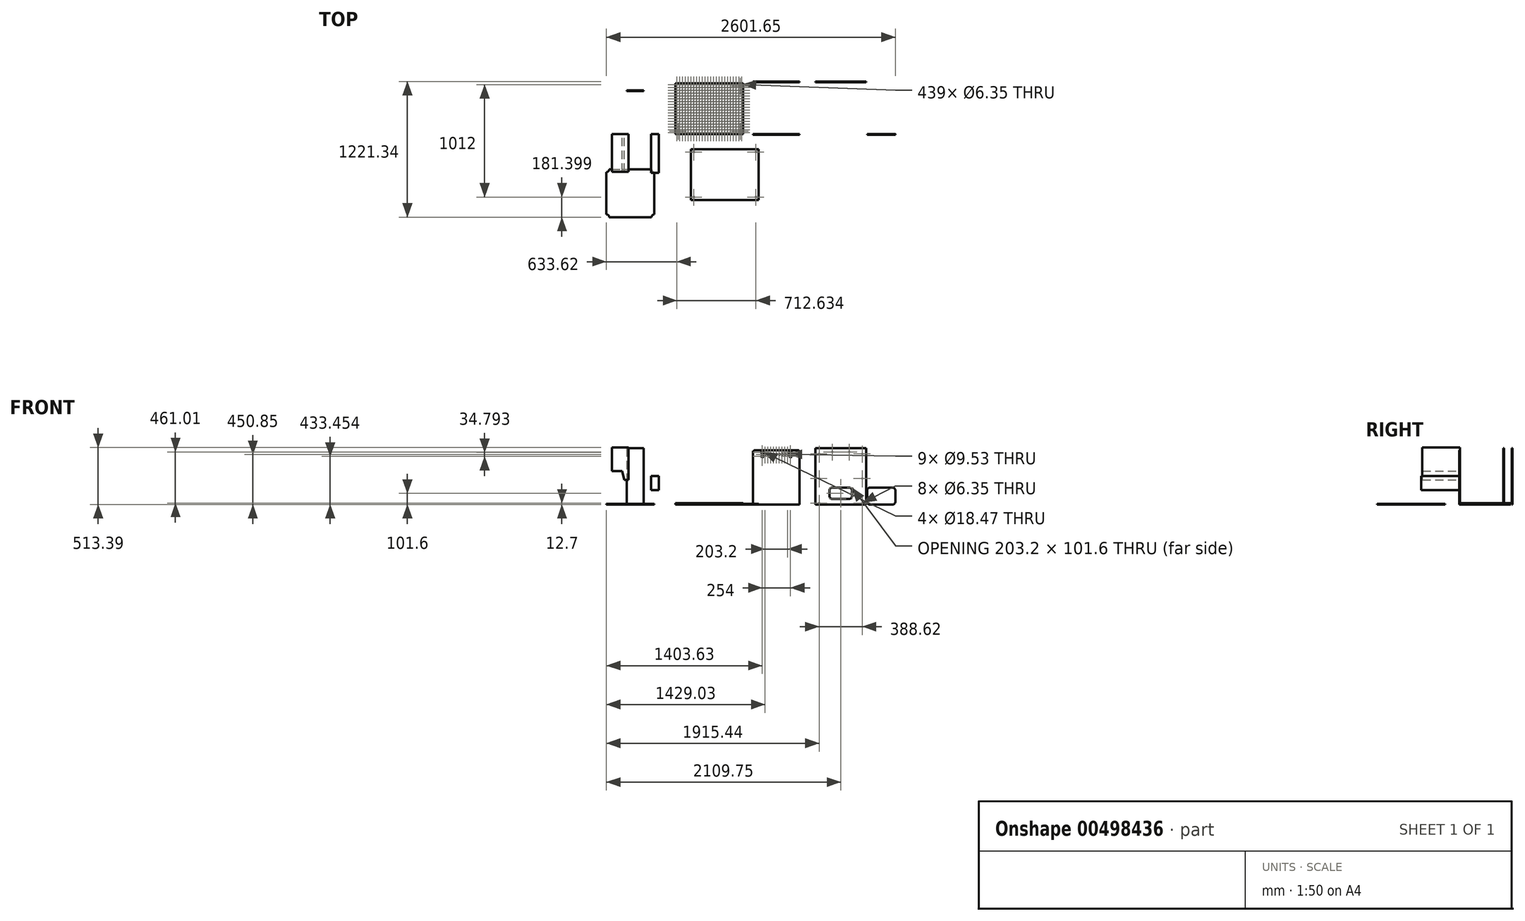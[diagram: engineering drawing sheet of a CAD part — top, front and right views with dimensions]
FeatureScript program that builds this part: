
annotation { "Feature Type Name" : "Feature", "Feature Type Description" : "" }
export const myFeature = defineFeature(function(context is Context, id is Id, definition is map)
    precondition{}
    {
        {
            var Q0;
            Q0=qCreatedBy(makeId("Top.planeOp"),FACE);
            var sketch = newSketch(context, id + "F0", { "sketchPlane" : qUnion([Q0])});
            skLineSegment(sketch, "E0.bottom", {"start": v(0, 0) * mm, "end": v(609.6, 0) * mm});
            skLineSegment(sketch, "E0.top", {"start": v(0, 457.2) * mm, "end": v(609.6, 457.2) * mm});
            skLineSegment(sketch, "E0.left", {"start": v(0, 0) * mm, "end": v(0, 457.2) * mm});
            skLineSegment(sketch, "E0.right", {"start": v(609.6, 0) * mm, "end": v(609.6, 457.2) * mm});
            skCircle(sketch, "E1", {"center": v(12.7, 444.5) * mm, "radius": 3.17 * mm});
            skCircle(sketch, "E2.0.1.0", {"center": v(12.7, 419.1) * mm, "radius": 3.17 * mm});
            skCircle(sketch, "E2.0.2.0", {"center": v(12.7, 393.7) * mm, "radius": 3.17 * mm});
            skCircle(sketch, "E2.0.3.0", {"center": v(12.7, 368.3) * mm, "radius": 3.17 * mm});
            skCircle(sketch, "E2.0.4.0", {"center": v(12.7, 342.9) * mm, "radius": 3.17 * mm});
            skCircle(sketch, "E2.0.5.0", {"center": v(12.7, 317.5) * mm, "radius": 3.17 * mm});
            skCircle(sketch, "E2.0.6.0", {"center": v(12.7, 292.1) * mm, "radius": 3.17 * mm});
            skCircle(sketch, "E2.0.7.0", {"center": v(12.7, 266.7) * mm, "radius": 3.17 * mm});
            skCircle(sketch, "E2.1.0.0", {"center": v(38.1, 444.5) * mm, "radius": 3.17 * mm});
            skCircle(sketch, "E2.1.1.0", {"center": v(38.1, 419.1) * mm, "radius": 3.17 * mm});
            skCircle(sketch, "E2.1.2.0", {"center": v(38.1, 393.7) * mm, "radius": 3.17 * mm});
            skCircle(sketch, "E2.1.3.0", {"center": v(38.1, 368.3) * mm, "radius": 3.17 * mm});
            skCircle(sketch, "E2.1.4.0", {"center": v(38.1, 342.9) * mm, "radius": 3.17 * mm});
            skCircle(sketch, "E2.1.5.0", {"center": v(38.1, 317.5) * mm, "radius": 3.17 * mm});
            skCircle(sketch, "E2.1.6.0", {"center": v(38.1, 292.1) * mm, "radius": 3.17 * mm});
            skCircle(sketch, "E2.1.7.0", {"center": v(38.1, 266.7) * mm, "radius": 3.17 * mm});
            skCircle(sketch, "E2.2.0.0", {"center": v(63.5, 444.5) * mm, "radius": 3.17 * mm});
            skCircle(sketch, "E2.2.1.0", {"center": v(63.5, 419.1) * mm, "radius": 3.17 * mm});
            skCircle(sketch, "E2.2.2.0", {"center": v(63.5, 393.7) * mm, "radius": 3.17 * mm});
            skCircle(sketch, "E2.2.3.0", {"center": v(63.5, 368.3) * mm, "radius": 3.17 * mm});
            skCircle(sketch, "E2.2.4.0", {"center": v(63.5, 342.9) * mm, "radius": 3.17 * mm});
            skCircle(sketch, "E2.2.5.0", {"center": v(63.5, 317.5) * mm, "radius": 3.17 * mm});
            skCircle(sketch, "E2.2.6.0", {"center": v(63.5, 292.1) * mm, "radius": 3.17 * mm});
            skCircle(sketch, "E2.2.7.0", {"center": v(63.5, 266.7) * mm, "radius": 3.17 * mm});
            skCircle(sketch, "E2.3.0.0", {"center": v(88.9, 444.5) * mm, "radius": 3.17 * mm});
            skCircle(sketch, "E2.3.1.0", {"center": v(88.9, 419.1) * mm, "radius": 3.17 * mm});
            skCircle(sketch, "E2.3.2.0", {"center": v(88.9, 393.7) * mm, "radius": 3.17 * mm});
            skCircle(sketch, "E2.3.3.0", {"center": v(88.9, 368.3) * mm, "radius": 3.17 * mm});
            skCircle(sketch, "E2.3.4.0", {"center": v(88.9, 342.9) * mm, "radius": 3.17 * mm});
            skCircle(sketch, "E2.3.5.0", {"center": v(88.9, 317.5) * mm, "radius": 3.17 * mm});
            skCircle(sketch, "E2.3.6.0", {"center": v(88.9, 292.1) * mm, "radius": 3.17 * mm});
            skCircle(sketch, "E2.3.7.0", {"center": v(88.9, 266.7) * mm, "radius": 3.17 * mm});
            skCircle(sketch, "E2.4.0.0", {"center": v(114.3, 444.5) * mm, "radius": 3.17 * mm});
            skCircle(sketch, "E2.4.1.0", {"center": v(114.3, 419.1) * mm, "radius": 3.17 * mm});
            skCircle(sketch, "E2.4.2.0", {"center": v(114.3, 393.7) * mm, "radius": 3.17 * mm});
            skCircle(sketch, "E2.4.3.0", {"center": v(114.3, 368.3) * mm, "radius": 3.17 * mm});
            skCircle(sketch, "E2.4.4.0", {"center": v(114.3, 342.9) * mm, "radius": 3.17 * mm});
            skCircle(sketch, "E2.4.5.0", {"center": v(114.3, 317.5) * mm, "radius": 3.17 * mm});
            skCircle(sketch, "E2.4.6.0", {"center": v(114.3, 292.1) * mm, "radius": 3.17 * mm});
            skCircle(sketch, "E2.4.7.0", {"center": v(114.3, 266.7) * mm, "radius": 3.17 * mm});
            skCircle(sketch, "E2.5.0.0", {"center": v(139.7, 444.5) * mm, "radius": 3.17 * mm});
            skCircle(sketch, "E2.5.1.0", {"center": v(139.7, 419.1) * mm, "radius": 3.17 * mm});
            skCircle(sketch, "E2.5.2.0", {"center": v(139.7, 393.7) * mm, "radius": 3.17 * mm});
            skCircle(sketch, "E2.5.3.0", {"center": v(139.7, 368.3) * mm, "radius": 3.17 * mm});
            skCircle(sketch, "E2.5.4.0", {"center": v(139.7, 342.9) * mm, "radius": 3.17 * mm});
            skCircle(sketch, "E2.5.5.0", {"center": v(139.7, 317.5) * mm, "radius": 3.17 * mm});
            skCircle(sketch, "E2.5.6.0", {"center": v(139.7, 292.1) * mm, "radius": 3.17 * mm});
            skCircle(sketch, "E2.5.7.0", {"center": v(139.7, 266.7) * mm, "radius": 3.17 * mm});
            skCircle(sketch, "E2.6.0.0", {"center": v(165.1, 444.5) * mm, "radius": 3.17 * mm});
            skCircle(sketch, "E2.6.1.0", {"center": v(165.1, 419.1) * mm, "radius": 3.17 * mm});
            skCircle(sketch, "E2.6.2.0", {"center": v(165.1, 393.7) * mm, "radius": 3.17 * mm});
            skCircle(sketch, "E2.6.3.0", {"center": v(165.1, 368.3) * mm, "radius": 3.17 * mm});
            skCircle(sketch, "E2.6.4.0", {"center": v(165.1, 342.9) * mm, "radius": 3.17 * mm});
            skCircle(sketch, "E2.6.5.0", {"center": v(165.1, 317.5) * mm, "radius": 3.17 * mm});
            skCircle(sketch, "E2.6.6.0", {"center": v(165.1, 292.1) * mm, "radius": 3.17 * mm});
            skCircle(sketch, "E2.6.7.0", {"center": v(165.1, 266.7) * mm, "radius": 3.17 * mm});
            skCircle(sketch, "E2.7.0.0", {"center": v(190.5, 444.5) * mm, "radius": 3.17 * mm});
            skCircle(sketch, "E2.7.1.0", {"center": v(190.5, 419.1) * mm, "radius": 3.17 * mm});
            skCircle(sketch, "E2.7.2.0", {"center": v(190.5, 393.7) * mm, "radius": 3.17 * mm});
            skCircle(sketch, "E2.7.3.0", {"center": v(190.5, 368.3) * mm, "radius": 3.17 * mm});
            skCircle(sketch, "E2.7.4.0", {"center": v(190.5, 342.9) * mm, "radius": 3.17 * mm});
            skCircle(sketch, "E2.7.5.0", {"center": v(190.5, 317.5) * mm, "radius": 3.17 * mm});
            skCircle(sketch, "E2.7.6.0", {"center": v(190.5, 292.1) * mm, "radius": 3.17 * mm});
            skCircle(sketch, "E2.7.7.0", {"center": v(190.5, 266.7) * mm, "radius": 3.17 * mm});
            skCircle(sketch, "E2.8.0.0", {"center": v(215.9, 444.5) * mm, "radius": 3.17 * mm});
            skCircle(sketch, "E2.8.1.0", {"center": v(215.9, 419.1) * mm, "radius": 3.17 * mm});
            skCircle(sketch, "E2.8.2.0", {"center": v(215.9, 393.7) * mm, "radius": 3.17 * mm});
            skCircle(sketch, "E2.8.3.0", {"center": v(215.9, 368.3) * mm, "radius": 3.17 * mm});
            skCircle(sketch, "E2.8.4.0", {"center": v(215.9, 342.9) * mm, "radius": 3.17 * mm});
            skCircle(sketch, "E2.8.5.0", {"center": v(215.9, 317.5) * mm, "radius": 3.17 * mm});
            skCircle(sketch, "E2.8.6.0", {"center": v(215.9, 292.1) * mm, "radius": 3.17 * mm});
            skCircle(sketch, "E2.8.7.0", {"center": v(215.9, 266.7) * mm, "radius": 3.17 * mm});
            skCircle(sketch, "E2.9.0.0", {"center": v(241.3, 444.5) * mm, "radius": 3.17 * mm});
            skCircle(sketch, "E2.9.1.0", {"center": v(241.3, 419.1) * mm, "radius": 3.17 * mm});
            skCircle(sketch, "E2.9.2.0", {"center": v(241.3, 393.7) * mm, "radius": 3.17 * mm});
            skCircle(sketch, "E2.9.3.0", {"center": v(241.3, 368.3) * mm, "radius": 3.17 * mm});
            skCircle(sketch, "E2.9.4.0", {"center": v(241.3, 342.9) * mm, "radius": 3.17 * mm});
            skCircle(sketch, "E2.9.5.0", {"center": v(241.3, 317.5) * mm, "radius": 3.17 * mm});
            skCircle(sketch, "E2.9.6.0", {"center": v(241.3, 292.1) * mm, "radius": 3.17 * mm});
            skCircle(sketch, "E2.9.7.0", {"center": v(241.3, 266.7) * mm, "radius": 3.17 * mm});
            skCircle(sketch, "E2.10.0.0", {"center": v(266.7, 444.5) * mm, "radius": 3.17 * mm});
            skCircle(sketch, "E2.10.1.0", {"center": v(266.7, 419.1) * mm, "radius": 3.17 * mm});
            skCircle(sketch, "E2.10.2.0", {"center": v(266.7, 393.7) * mm, "radius": 3.17 * mm});
            skCircle(sketch, "E2.10.3.0", {"center": v(266.7, 368.3) * mm, "radius": 3.17 * mm});
            skCircle(sketch, "E2.10.4.0", {"center": v(266.7, 342.9) * mm, "radius": 3.17 * mm});
            skCircle(sketch, "E2.10.5.0", {"center": v(266.7, 317.5) * mm, "radius": 3.17 * mm});
            skCircle(sketch, "E2.10.6.0", {"center": v(266.7, 292.1) * mm, "radius": 3.17 * mm});
            skCircle(sketch, "E2.10.7.0", {"center": v(266.7, 266.7) * mm, "radius": 3.17 * mm});
            skCircle(sketch, "E2.11.0.0", {"center": v(292.1, 444.5) * mm, "radius": 3.17 * mm});
            skCircle(sketch, "E2.11.1.0", {"center": v(292.1, 419.1) * mm, "radius": 3.17 * mm});
            skCircle(sketch, "E2.11.2.0", {"center": v(292.1, 393.7) * mm, "radius": 3.17 * mm});
            skCircle(sketch, "E2.11.3.0", {"center": v(292.1, 368.3) * mm, "radius": 3.17 * mm});
            skCircle(sketch, "E2.11.4.0", {"center": v(292.1, 342.9) * mm, "radius": 3.17 * mm});
            skCircle(sketch, "E2.11.5.0", {"center": v(292.1, 317.5) * mm, "radius": 3.17 * mm});
            skCircle(sketch, "E2.11.6.0", {"center": v(292.1, 292.1) * mm, "radius": 3.17 * mm});
            skCircle(sketch, "E2.11.7.0", {"center": v(292.1, 266.7) * mm, "radius": 3.17 * mm});
            skCircle(sketch, "E2.12.0.0", {"center": v(317.5, 444.5) * mm, "radius": 3.17 * mm});
            skCircle(sketch, "E2.12.1.0", {"center": v(317.5, 419.1) * mm, "radius": 3.17 * mm});
            skCircle(sketch, "E2.12.2.0", {"center": v(317.5, 393.7) * mm, "radius": 3.17 * mm});
            skCircle(sketch, "E2.12.3.0", {"center": v(317.5, 368.3) * mm, "radius": 3.17 * mm});
            skCircle(sketch, "E2.12.4.0", {"center": v(317.5, 342.9) * mm, "radius": 3.17 * mm});
            skCircle(sketch, "E2.12.5.0", {"center": v(317.5, 317.5) * mm, "radius": 3.17 * mm});
            skCircle(sketch, "E2.12.6.0", {"center": v(317.5, 292.1) * mm, "radius": 3.17 * mm});
            skCircle(sketch, "E2.12.7.0", {"center": v(317.5, 266.7) * mm, "radius": 3.17 * mm});
            skCircle(sketch, "E2.13.0.0", {"center": v(342.9, 444.5) * mm, "radius": 3.17 * mm});
            skCircle(sketch, "E2.13.1.0", {"center": v(342.9, 419.1) * mm, "radius": 3.17 * mm});
            skCircle(sketch, "E2.13.2.0", {"center": v(342.9, 393.7) * mm, "radius": 3.17 * mm});
            skCircle(sketch, "E2.13.3.0", {"center": v(342.9, 368.3) * mm, "radius": 3.17 * mm});
            skCircle(sketch, "E2.13.4.0", {"center": v(342.9, 342.9) * mm, "radius": 3.17 * mm});
            skCircle(sketch, "E2.13.5.0", {"center": v(342.9, 317.5) * mm, "radius": 3.17 * mm});
            skCircle(sketch, "E2.13.6.0", {"center": v(342.9, 292.1) * mm, "radius": 3.17 * mm});
            skCircle(sketch, "E2.13.7.0", {"center": v(342.9, 266.7) * mm, "radius": 3.17 * mm});
            skCircle(sketch, "E2.14.0.0", {"center": v(368.3, 444.5) * mm, "radius": 3.17 * mm});
            skCircle(sketch, "E2.14.1.0", {"center": v(368.3, 419.1) * mm, "radius": 3.17 * mm});
            skCircle(sketch, "E2.14.2.0", {"center": v(368.3, 393.7) * mm, "radius": 3.17 * mm});
            skCircle(sketch, "E2.14.3.0", {"center": v(368.3, 368.3) * mm, "radius": 3.17 * mm});
            skCircle(sketch, "E2.14.4.0", {"center": v(368.3, 342.9) * mm, "radius": 3.17 * mm});
            skCircle(sketch, "E2.14.5.0", {"center": v(368.3, 317.5) * mm, "radius": 3.17 * mm});
            skCircle(sketch, "E2.14.6.0", {"center": v(368.3, 292.1) * mm, "radius": 3.17 * mm});
            skCircle(sketch, "E2.14.7.0", {"center": v(368.3, 266.7) * mm, "radius": 3.17 * mm});
            skCircle(sketch, "E2.15.0.0", {"center": v(393.7, 444.5) * mm, "radius": 3.17 * mm});
            skCircle(sketch, "E2.15.1.0", {"center": v(393.7, 419.1) * mm, "radius": 3.17 * mm});
            skCircle(sketch, "E2.15.2.0", {"center": v(393.7, 393.7) * mm, "radius": 3.17 * mm});
            skCircle(sketch, "E2.15.3.0", {"center": v(393.7, 368.3) * mm, "radius": 3.17 * mm});
            skCircle(sketch, "E2.15.4.0", {"center": v(393.7, 342.9) * mm, "radius": 3.17 * mm});
            skCircle(sketch, "E2.15.5.0", {"center": v(393.7, 317.5) * mm, "radius": 3.17 * mm});
            skCircle(sketch, "E2.15.6.0", {"center": v(393.7, 292.1) * mm, "radius": 3.17 * mm});
            skCircle(sketch, "E2.15.7.0", {"center": v(393.7, 266.7) * mm, "radius": 3.17 * mm});
            skCircle(sketch, "E2.16.0.0", {"center": v(419.1, 444.5) * mm, "radius": 3.17 * mm});
            skCircle(sketch, "E2.16.1.0", {"center": v(419.1, 419.1) * mm, "radius": 3.17 * mm});
            skCircle(sketch, "E2.16.2.0", {"center": v(419.1, 393.7) * mm, "radius": 3.17 * mm});
            skCircle(sketch, "E2.16.3.0", {"center": v(419.1, 368.3) * mm, "radius": 3.17 * mm});
            skCircle(sketch, "E2.16.4.0", {"center": v(419.1, 342.9) * mm, "radius": 3.17 * mm});
            skCircle(sketch, "E2.16.5.0", {"center": v(419.1, 317.5) * mm, "radius": 3.17 * mm});
            skCircle(sketch, "E2.16.6.0", {"center": v(419.1, 292.1) * mm, "radius": 3.17 * mm});
            skCircle(sketch, "E2.16.7.0", {"center": v(419.1, 266.7) * mm, "radius": 3.17 * mm});
            skCircle(sketch, "E2.17.0.0", {"center": v(444.5, 444.5) * mm, "radius": 3.17 * mm});
            skCircle(sketch, "E2.17.1.0", {"center": v(444.5, 419.1) * mm, "radius": 3.17 * mm});
            skCircle(sketch, "E2.17.2.0", {"center": v(444.5, 393.7) * mm, "radius": 3.17 * mm});
            skCircle(sketch, "E2.17.3.0", {"center": v(444.5, 368.3) * mm, "radius": 3.17 * mm});
            skCircle(sketch, "E2.17.4.0", {"center": v(444.5, 342.9) * mm, "radius": 3.17 * mm});
            skCircle(sketch, "E2.17.5.0", {"center": v(444.5, 317.5) * mm, "radius": 3.17 * mm});
            skCircle(sketch, "E2.17.6.0", {"center": v(444.5, 292.1) * mm, "radius": 3.17 * mm});
            skCircle(sketch, "E2.17.7.0", {"center": v(444.5, 266.7) * mm, "radius": 3.17 * mm});
            skCircle(sketch, "E2.18.0.0", {"center": v(469.9, 444.5) * mm, "radius": 3.17 * mm});
            skCircle(sketch, "E2.18.1.0", {"center": v(469.9, 419.1) * mm, "radius": 3.17 * mm});
            skCircle(sketch, "E2.18.2.0", {"center": v(469.9, 393.7) * mm, "radius": 3.17 * mm});
            skCircle(sketch, "E2.18.3.0", {"center": v(469.9, 368.3) * mm, "radius": 3.17 * mm});
            skCircle(sketch, "E2.18.4.0", {"center": v(469.9, 342.9) * mm, "radius": 3.17 * mm});
            skCircle(sketch, "E2.18.5.0", {"center": v(469.9, 317.5) * mm, "radius": 3.17 * mm});
            skCircle(sketch, "E2.18.6.0", {"center": v(469.9, 292.1) * mm, "radius": 3.17 * mm});
            skCircle(sketch, "E2.18.7.0", {"center": v(469.9, 266.7) * mm, "radius": 3.17 * mm});
            skCircle(sketch, "E2.19.0.0", {"center": v(495.3, 444.5) * mm, "radius": 3.17 * mm});
            skCircle(sketch, "E2.19.1.0", {"center": v(495.3, 419.1) * mm, "radius": 3.17 * mm});
            skCircle(sketch, "E2.19.2.0", {"center": v(495.3, 393.7) * mm, "radius": 3.17 * mm});
            skCircle(sketch, "E2.19.3.0", {"center": v(495.3, 368.3) * mm, "radius": 3.17 * mm});
            skCircle(sketch, "E2.19.4.0", {"center": v(495.3, 342.9) * mm, "radius": 3.17 * mm});
            skCircle(sketch, "E2.19.5.0", {"center": v(495.3, 317.5) * mm, "radius": 3.17 * mm});
            skCircle(sketch, "E2.19.6.0", {"center": v(495.3, 292.1) * mm, "radius": 3.17 * mm});
            skCircle(sketch, "E2.19.7.0", {"center": v(495.3, 266.7) * mm, "radius": 3.17 * mm});
            skCircle(sketch, "E2.20.0.0", {"center": v(520.7, 444.5) * mm, "radius": 3.17 * mm});
            skCircle(sketch, "E2.20.1.0", {"center": v(520.7, 419.1) * mm, "radius": 3.17 * mm});
            skCircle(sketch, "E2.20.2.0", {"center": v(520.7, 393.7) * mm, "radius": 3.17 * mm});
            skCircle(sketch, "E2.20.3.0", {"center": v(520.7, 368.3) * mm, "radius": 3.17 * mm});
            skCircle(sketch, "E2.20.4.0", {"center": v(520.7, 342.9) * mm, "radius": 3.17 * mm});
            skCircle(sketch, "E2.20.5.0", {"center": v(520.7, 317.5) * mm, "radius": 3.17 * mm});
            skCircle(sketch, "E2.20.6.0", {"center": v(520.7, 292.1) * mm, "radius": 3.17 * mm});
            skCircle(sketch, "E2.20.7.0", {"center": v(520.7, 266.7) * mm, "radius": 3.17 * mm});
            skCircle(sketch, "E2.21.0.0", {"center": v(546.1, 444.5) * mm, "radius": 3.17 * mm});
            skCircle(sketch, "E2.21.1.0", {"center": v(546.1, 419.1) * mm, "radius": 3.17 * mm});
            skCircle(sketch, "E2.21.2.0", {"center": v(546.1, 393.7) * mm, "radius": 3.17 * mm});
            skCircle(sketch, "E2.21.3.0", {"center": v(546.1, 368.3) * mm, "radius": 3.17 * mm});
            skCircle(sketch, "E2.21.4.0", {"center": v(546.1, 342.9) * mm, "radius": 3.17 * mm});
            skCircle(sketch, "E2.21.5.0", {"center": v(546.1, 317.5) * mm, "radius": 3.17 * mm});
            skCircle(sketch, "E2.21.6.0", {"center": v(546.1, 292.1) * mm, "radius": 3.17 * mm});
            skCircle(sketch, "E2.21.7.0", {"center": v(546.1, 266.7) * mm, "radius": 3.17 * mm});
            skCircle(sketch, "E2.22.0.0", {"center": v(571.5, 444.5) * mm, "radius": 3.17 * mm});
            skCircle(sketch, "E2.22.1.0", {"center": v(571.5, 419.1) * mm, "radius": 3.17 * mm});
            skCircle(sketch, "E2.22.2.0", {"center": v(571.5, 393.7) * mm, "radius": 3.17 * mm});
            skCircle(sketch, "E2.22.3.0", {"center": v(571.5, 368.3) * mm, "radius": 3.17 * mm});
            skCircle(sketch, "E2.22.4.0", {"center": v(571.5, 342.9) * mm, "radius": 3.17 * mm});
            skCircle(sketch, "E2.22.5.0", {"center": v(571.5, 317.5) * mm, "radius": 3.17 * mm});
            skCircle(sketch, "E2.22.6.0", {"center": v(571.5, 292.1) * mm, "radius": 3.17 * mm});
            skCircle(sketch, "E2.22.7.0", {"center": v(571.5, 266.7) * mm, "radius": 3.17 * mm});
            skLineSegment(sketch, "E2.direction1", {"start": v(12.7, 444.5) * mm, "end": v(38.1, 444.5) * mm, "construction": true});
            skLineSegment(sketch, "E2.direction2", {"start": v(12.7, 444.5) * mm, "end": v(12.7, 419.1) * mm, "construction": true});
            skCircle(sketch, "E3.0.23.0", {"center": v(596.9, 444.5) * mm, "radius": 3.17 * mm});
            skCircle(sketch, "E3.0.23.1", {"center": v(596.9, 419.1) * mm, "radius": 3.17 * mm});
            skCircle(sketch, "E3.0.23.2", {"center": v(596.9, 393.7) * mm, "radius": 3.17 * mm});
            skCircle(sketch, "E3.0.23.3", {"center": v(596.9, 368.3) * mm, "radius": 3.17 * mm});
            skCircle(sketch, "E3.0.23.4", {"center": v(596.9, 342.9) * mm, "radius": 3.17 * mm});
            skCircle(sketch, "E3.0.23.5", {"center": v(596.9, 317.5) * mm, "radius": 3.17 * mm});
            skCircle(sketch, "E3.0.23.6", {"center": v(596.9, 292.1) * mm, "radius": 3.17 * mm});
            skCircle(sketch, "E3.0.23.7", {"center": v(596.9, 266.7) * mm, "radius": 3.17 * mm});
            skCircle(sketch, "E4.0.0.8", {"center": v(12.7, 241.3) * mm, "radius": 3.17 * mm});
            skCircle(sketch, "E4.0.0.9", {"center": v(12.7, 215.9) * mm, "radius": 3.17 * mm});
            skCircle(sketch, "E4.0.0.10", {"center": v(12.7, 190.5) * mm, "radius": 3.17 * mm});
            skCircle(sketch, "E4.0.0.11", {"center": v(12.7, 165.1) * mm, "radius": 3.17 * mm});
            skCircle(sketch, "E4.0.0.12", {"center": v(12.7, 139.7) * mm, "radius": 3.17 * mm});
            skCircle(sketch, "E4.0.0.13", {"center": v(12.7, 114.3) * mm, "radius": 3.17 * mm});
            skCircle(sketch, "E4.0.0.14", {"center": v(12.7, 88.9) * mm, "radius": 3.17 * mm});
            skCircle(sketch, "E4.0.0.15", {"center": v(12.7, 63.5) * mm, "radius": 3.17 * mm});
            skCircle(sketch, "E4.0.0.16", {"center": v(12.7, 38.1) * mm, "radius": 3.17 * mm});
            skCircle(sketch, "E4.0.0.17", {"center": v(12.7, 12.7) * mm, "radius": 3.17 * mm});
            skCircle(sketch, "E4.0.1.8", {"center": v(38.1, 241.3) * mm, "radius": 3.17 * mm});
            skCircle(sketch, "E4.0.1.9", {"center": v(38.1, 215.9) * mm, "radius": 3.17 * mm});
            skCircle(sketch, "E4.0.1.10", {"center": v(38.1, 190.5) * mm, "radius": 3.17 * mm});
            skCircle(sketch, "E4.0.1.11", {"center": v(38.1, 165.1) * mm, "radius": 3.17 * mm});
            skCircle(sketch, "E4.0.1.12", {"center": v(38.1, 139.7) * mm, "radius": 3.17 * mm});
            skCircle(sketch, "E4.0.1.13", {"center": v(38.1, 114.3) * mm, "radius": 3.17 * mm});
            skCircle(sketch, "E4.0.1.14", {"center": v(38.1, 88.9) * mm, "radius": 3.17 * mm});
            skCircle(sketch, "E4.0.1.15", {"center": v(38.1, 63.5) * mm, "radius": 3.17 * mm});
            skCircle(sketch, "E4.0.1.16", {"center": v(38.1, 38.1) * mm, "radius": 3.17 * mm});
            skCircle(sketch, "E4.0.1.17", {"center": v(38.1, 12.7) * mm, "radius": 3.17 * mm});
            skCircle(sketch, "E4.0.2.8", {"center": v(63.5, 241.3) * mm, "radius": 3.17 * mm});
            skCircle(sketch, "E4.0.2.9", {"center": v(63.5, 215.9) * mm, "radius": 3.17 * mm});
            skCircle(sketch, "E4.0.2.10", {"center": v(63.5, 190.5) * mm, "radius": 3.17 * mm});
            skCircle(sketch, "E4.0.2.11", {"center": v(63.5, 165.1) * mm, "radius": 3.17 * mm});
            skCircle(sketch, "E4.0.2.12", {"center": v(63.5, 139.7) * mm, "radius": 3.17 * mm});
            skCircle(sketch, "E4.0.2.13", {"center": v(63.5, 114.3) * mm, "radius": 3.17 * mm});
            skCircle(sketch, "E4.0.2.14", {"center": v(63.5, 88.9) * mm, "radius": 3.17 * mm});
            skCircle(sketch, "E4.0.2.15", {"center": v(63.5, 63.5) * mm, "radius": 3.17 * mm});
            skCircle(sketch, "E4.0.2.16", {"center": v(63.5, 38.1) * mm, "radius": 3.17 * mm});
            skCircle(sketch, "E4.0.2.17", {"center": v(63.5, 12.7) * mm, "radius": 3.17 * mm});
            skCircle(sketch, "E4.0.3.8", {"center": v(88.9, 241.3) * mm, "radius": 3.17 * mm});
            skCircle(sketch, "E4.0.3.9", {"center": v(88.9, 215.9) * mm, "radius": 3.17 * mm});
            skCircle(sketch, "E4.0.3.10", {"center": v(88.9, 190.5) * mm, "radius": 3.17 * mm});
            skCircle(sketch, "E4.0.3.11", {"center": v(88.9, 165.1) * mm, "radius": 3.17 * mm});
            skCircle(sketch, "E4.0.3.12", {"center": v(88.9, 139.7) * mm, "radius": 3.17 * mm});
            skCircle(sketch, "E4.0.3.13", {"center": v(88.9, 114.3) * mm, "radius": 3.17 * mm});
            skCircle(sketch, "E4.0.3.14", {"center": v(88.9, 88.9) * mm, "radius": 3.17 * mm});
            skCircle(sketch, "E4.0.3.15", {"center": v(88.9, 63.5) * mm, "radius": 3.17 * mm});
            skCircle(sketch, "E4.0.3.16", {"center": v(88.9, 38.1) * mm, "radius": 3.17 * mm});
            skCircle(sketch, "E4.0.3.17", {"center": v(88.9, 12.7) * mm, "radius": 3.17 * mm});
            skCircle(sketch, "E4.0.4.8", {"center": v(114.3, 241.3) * mm, "radius": 3.17 * mm});
            skCircle(sketch, "E4.0.4.9", {"center": v(114.3, 215.9) * mm, "radius": 3.17 * mm});
            skCircle(sketch, "E4.0.4.10", {"center": v(114.3, 190.5) * mm, "radius": 3.17 * mm});
            skCircle(sketch, "E4.0.4.11", {"center": v(114.3, 165.1) * mm, "radius": 3.17 * mm});
            skCircle(sketch, "E4.0.4.12", {"center": v(114.3, 139.7) * mm, "radius": 3.17 * mm});
            skCircle(sketch, "E4.0.4.13", {"center": v(114.3, 114.3) * mm, "radius": 3.17 * mm});
            skCircle(sketch, "E4.0.4.14", {"center": v(114.3, 88.9) * mm, "radius": 3.17 * mm});
            skCircle(sketch, "E4.0.4.15", {"center": v(114.3, 63.5) * mm, "radius": 3.17 * mm});
            skCircle(sketch, "E4.0.4.16", {"center": v(114.3, 38.1) * mm, "radius": 3.17 * mm});
            skCircle(sketch, "E4.0.4.17", {"center": v(114.3, 12.7) * mm, "radius": 3.17 * mm});
            skCircle(sketch, "E4.0.5.8", {"center": v(139.7, 241.3) * mm, "radius": 3.17 * mm});
            skCircle(sketch, "E4.0.5.9", {"center": v(139.7, 215.9) * mm, "radius": 3.17 * mm});
            skCircle(sketch, "E4.0.5.10", {"center": v(139.7, 190.5) * mm, "radius": 3.17 * mm});
            skCircle(sketch, "E4.0.5.11", {"center": v(139.7, 165.1) * mm, "radius": 3.17 * mm});
            skCircle(sketch, "E4.0.5.12", {"center": v(139.7, 139.7) * mm, "radius": 3.17 * mm});
            skCircle(sketch, "E4.0.5.13", {"center": v(139.7, 114.3) * mm, "radius": 3.17 * mm});
            skCircle(sketch, "E4.0.5.14", {"center": v(139.7, 88.9) * mm, "radius": 3.17 * mm});
            skCircle(sketch, "E4.0.5.15", {"center": v(139.7, 63.5) * mm, "radius": 3.17 * mm});
            skCircle(sketch, "E4.0.5.16", {"center": v(139.7, 38.1) * mm, "radius": 3.17 * mm});
            skCircle(sketch, "E4.0.5.17", {"center": v(139.7, 12.7) * mm, "radius": 3.17 * mm});
            skCircle(sketch, "E4.0.6.8", {"center": v(165.1, 241.3) * mm, "radius": 3.17 * mm});
            skCircle(sketch, "E4.0.6.9", {"center": v(165.1, 215.9) * mm, "radius": 3.17 * mm});
            skCircle(sketch, "E4.0.6.10", {"center": v(165.1, 190.5) * mm, "radius": 3.17 * mm});
            skCircle(sketch, "E4.0.6.11", {"center": v(165.1, 165.1) * mm, "radius": 3.17 * mm});
            skCircle(sketch, "E4.0.6.12", {"center": v(165.1, 139.7) * mm, "radius": 3.17 * mm});
            skCircle(sketch, "E4.0.6.13", {"center": v(165.1, 114.3) * mm, "radius": 3.17 * mm});
            skCircle(sketch, "E4.0.6.14", {"center": v(165.1, 88.9) * mm, "radius": 3.17 * mm});
            skCircle(sketch, "E4.0.6.15", {"center": v(165.1, 63.5) * mm, "radius": 3.17 * mm});
            skCircle(sketch, "E4.0.6.16", {"center": v(165.1, 38.1) * mm, "radius": 3.17 * mm});
            skCircle(sketch, "E4.0.6.17", {"center": v(165.1, 12.7) * mm, "radius": 3.17 * mm});
            skCircle(sketch, "E4.0.7.8", {"center": v(190.5, 241.3) * mm, "radius": 3.17 * mm});
            skCircle(sketch, "E4.0.7.9", {"center": v(190.5, 215.9) * mm, "radius": 3.17 * mm});
            skCircle(sketch, "E4.0.7.10", {"center": v(190.5, 190.5) * mm, "radius": 3.17 * mm});
            skCircle(sketch, "E4.0.7.11", {"center": v(190.5, 165.1) * mm, "radius": 3.17 * mm});
            skCircle(sketch, "E4.0.7.12", {"center": v(190.5, 139.7) * mm, "radius": 3.17 * mm});
            skCircle(sketch, "E4.0.7.13", {"center": v(190.5, 114.3) * mm, "radius": 3.17 * mm});
            skCircle(sketch, "E4.0.7.14", {"center": v(190.5, 88.9) * mm, "radius": 3.17 * mm});
            skCircle(sketch, "E4.0.7.15", {"center": v(190.5, 63.5) * mm, "radius": 3.17 * mm});
            skCircle(sketch, "E4.0.7.16", {"center": v(190.5, 38.1) * mm, "radius": 3.17 * mm});
            skCircle(sketch, "E4.0.7.17", {"center": v(190.5, 12.7) * mm, "radius": 3.17 * mm});
            skCircle(sketch, "E4.0.8.8", {"center": v(215.9, 241.3) * mm, "radius": 3.17 * mm});
            skCircle(sketch, "E4.0.8.9", {"center": v(215.9, 215.9) * mm, "radius": 3.17 * mm});
            skCircle(sketch, "E4.0.8.10", {"center": v(215.9, 190.5) * mm, "radius": 3.17 * mm});
            skCircle(sketch, "E4.0.8.11", {"center": v(215.9, 165.1) * mm, "radius": 3.17 * mm});
            skCircle(sketch, "E4.0.8.12", {"center": v(215.9, 139.7) * mm, "radius": 3.17 * mm});
            skCircle(sketch, "E4.0.8.13", {"center": v(215.9, 114.3) * mm, "radius": 3.17 * mm});
            skCircle(sketch, "E4.0.8.14", {"center": v(215.9, 88.9) * mm, "radius": 3.17 * mm});
            skCircle(sketch, "E4.0.8.15", {"center": v(215.9, 63.5) * mm, "radius": 3.17 * mm});
            skCircle(sketch, "E4.0.8.16", {"center": v(215.9, 38.1) * mm, "radius": 3.17 * mm});
            skCircle(sketch, "E4.0.8.17", {"center": v(215.9, 12.7) * mm, "radius": 3.17 * mm});
            skCircle(sketch, "E4.0.9.8", {"center": v(241.3, 241.3) * mm, "radius": 3.17 * mm});
            skCircle(sketch, "E4.0.9.9", {"center": v(241.3, 215.9) * mm, "radius": 3.17 * mm});
            skCircle(sketch, "E4.0.9.10", {"center": v(241.3, 190.5) * mm, "radius": 3.17 * mm});
            skCircle(sketch, "E4.0.9.11", {"center": v(241.3, 165.1) * mm, "radius": 3.17 * mm});
            skCircle(sketch, "E4.0.9.12", {"center": v(241.3, 139.7) * mm, "radius": 3.17 * mm});
            skCircle(sketch, "E4.0.9.13", {"center": v(241.3, 114.3) * mm, "radius": 3.17 * mm});
            skCircle(sketch, "E4.0.9.14", {"center": v(241.3, 88.9) * mm, "radius": 3.17 * mm});
            skCircle(sketch, "E4.0.9.15", {"center": v(241.3, 63.5) * mm, "radius": 3.17 * mm});
            skCircle(sketch, "E4.0.9.16", {"center": v(241.3, 38.1) * mm, "radius": 3.17 * mm});
            skCircle(sketch, "E4.0.9.17", {"center": v(241.3, 12.7) * mm, "radius": 3.17 * mm});
            skCircle(sketch, "E4.0.10.8", {"center": v(266.7, 241.3) * mm, "radius": 3.17 * mm});
            skCircle(sketch, "E4.0.10.9", {"center": v(266.7, 215.9) * mm, "radius": 3.17 * mm});
            skCircle(sketch, "E4.0.10.10", {"center": v(266.7, 190.5) * mm, "radius": 3.17 * mm});
            skCircle(sketch, "E4.0.10.11", {"center": v(266.7, 165.1) * mm, "radius": 3.17 * mm});
            skCircle(sketch, "E4.0.10.12", {"center": v(266.7, 139.7) * mm, "radius": 3.17 * mm});
            skCircle(sketch, "E4.0.10.13", {"center": v(266.7, 114.3) * mm, "radius": 3.17 * mm});
            skCircle(sketch, "E4.0.10.14", {"center": v(266.7, 88.9) * mm, "radius": 3.17 * mm});
            skCircle(sketch, "E4.0.10.15", {"center": v(266.7, 63.5) * mm, "radius": 3.17 * mm});
            skCircle(sketch, "E4.0.10.16", {"center": v(266.7, 38.1) * mm, "radius": 3.17 * mm});
            skCircle(sketch, "E4.0.10.17", {"center": v(266.7, 12.7) * mm, "radius": 3.17 * mm});
            skCircle(sketch, "E4.0.11.8", {"center": v(292.1, 241.3) * mm, "radius": 3.17 * mm});
            skCircle(sketch, "E4.0.11.9", {"center": v(292.1, 215.9) * mm, "radius": 3.17 * mm});
            skCircle(sketch, "E4.0.11.10", {"center": v(292.1, 190.5) * mm, "radius": 3.17 * mm});
            skCircle(sketch, "E4.0.11.11", {"center": v(292.1, 165.1) * mm, "radius": 3.17 * mm});
            skCircle(sketch, "E4.0.11.12", {"center": v(292.1, 139.7) * mm, "radius": 3.17 * mm});
            skCircle(sketch, "E4.0.11.13", {"center": v(292.1, 114.3) * mm, "radius": 3.17 * mm});
            skCircle(sketch, "E4.0.11.14", {"center": v(292.1, 88.9) * mm, "radius": 3.17 * mm});
            skCircle(sketch, "E4.0.11.15", {"center": v(292.1, 63.5) * mm, "radius": 3.17 * mm});
            skCircle(sketch, "E4.0.11.16", {"center": v(292.1, 38.1) * mm, "radius": 3.17 * mm});
            skCircle(sketch, "E4.0.11.17", {"center": v(292.1, 12.7) * mm, "radius": 3.17 * mm});
            skCircle(sketch, "E4.0.12.8", {"center": v(317.5, 241.3) * mm, "radius": 3.17 * mm});
            skCircle(sketch, "E4.0.12.9", {"center": v(317.5, 215.9) * mm, "radius": 3.17 * mm});
            skCircle(sketch, "E4.0.12.10", {"center": v(317.5, 190.5) * mm, "radius": 3.17 * mm});
            skCircle(sketch, "E4.0.12.11", {"center": v(317.5, 165.1) * mm, "radius": 3.17 * mm});
            skCircle(sketch, "E4.0.12.12", {"center": v(317.5, 139.7) * mm, "radius": 3.17 * mm});
            skCircle(sketch, "E4.0.12.13", {"center": v(317.5, 114.3) * mm, "radius": 3.17 * mm});
            skCircle(sketch, "E4.0.12.14", {"center": v(317.5, 88.9) * mm, "radius": 3.17 * mm});
            skCircle(sketch, "E4.0.12.15", {"center": v(317.5, 63.5) * mm, "radius": 3.17 * mm});
            skCircle(sketch, "E4.0.12.16", {"center": v(317.5, 38.1) * mm, "radius": 3.17 * mm});
            skCircle(sketch, "E4.0.12.17", {"center": v(317.5, 12.7) * mm, "radius": 3.17 * mm});
            skCircle(sketch, "E4.0.13.8", {"center": v(342.9, 241.3) * mm, "radius": 3.17 * mm});
            skCircle(sketch, "E4.0.13.9", {"center": v(342.9, 215.9) * mm, "radius": 3.17 * mm});
            skCircle(sketch, "E4.0.13.10", {"center": v(342.9, 190.5) * mm, "radius": 3.17 * mm});
            skCircle(sketch, "E4.0.13.11", {"center": v(342.9, 165.1) * mm, "radius": 3.17 * mm});
            skCircle(sketch, "E4.0.13.12", {"center": v(342.9, 139.7) * mm, "radius": 3.17 * mm});
            skCircle(sketch, "E4.0.13.13", {"center": v(342.9, 114.3) * mm, "radius": 3.17 * mm});
            skCircle(sketch, "E4.0.13.14", {"center": v(342.9, 88.9) * mm, "radius": 3.17 * mm});
            skCircle(sketch, "E4.0.13.15", {"center": v(342.9, 63.5) * mm, "radius": 3.17 * mm});
            skCircle(sketch, "E4.0.13.16", {"center": v(342.9, 38.1) * mm, "radius": 3.17 * mm});
            skCircle(sketch, "E4.0.13.17", {"center": v(342.9, 12.7) * mm, "radius": 3.17 * mm});
            skCircle(sketch, "E4.0.14.8", {"center": v(368.3, 241.3) * mm, "radius": 3.17 * mm});
            skCircle(sketch, "E4.0.14.9", {"center": v(368.3, 215.9) * mm, "radius": 3.17 * mm});
            skCircle(sketch, "E4.0.14.10", {"center": v(368.3, 190.5) * mm, "radius": 3.17 * mm});
            skCircle(sketch, "E4.0.14.11", {"center": v(368.3, 165.1) * mm, "radius": 3.17 * mm});
            skCircle(sketch, "E4.0.14.12", {"center": v(368.3, 139.7) * mm, "radius": 3.17 * mm});
            skCircle(sketch, "E4.0.14.13", {"center": v(368.3, 114.3) * mm, "radius": 3.17 * mm});
            skCircle(sketch, "E4.0.14.14", {"center": v(368.3, 88.9) * mm, "radius": 3.17 * mm});
            skCircle(sketch, "E4.0.14.15", {"center": v(368.3, 63.5) * mm, "radius": 3.17 * mm});
            skCircle(sketch, "E4.0.14.16", {"center": v(368.3, 38.1) * mm, "radius": 3.17 * mm});
            skCircle(sketch, "E4.0.14.17", {"center": v(368.3, 12.7) * mm, "radius": 3.17 * mm});
            skCircle(sketch, "E4.0.15.8", {"center": v(393.7, 241.3) * mm, "radius": 3.17 * mm});
            skCircle(sketch, "E4.0.15.9", {"center": v(393.7, 215.9) * mm, "radius": 3.17 * mm});
            skCircle(sketch, "E4.0.15.10", {"center": v(393.7, 190.5) * mm, "radius": 3.17 * mm});
            skCircle(sketch, "E4.0.15.11", {"center": v(393.7, 165.1) * mm, "radius": 3.17 * mm});
            skCircle(sketch, "E4.0.15.12", {"center": v(393.7, 139.7) * mm, "radius": 3.17 * mm});
            skCircle(sketch, "E4.0.15.13", {"center": v(393.7, 114.3) * mm, "radius": 3.17 * mm});
            skCircle(sketch, "E4.0.15.14", {"center": v(393.7, 88.9) * mm, "radius": 3.17 * mm});
            skCircle(sketch, "E4.0.15.15", {"center": v(393.7, 63.5) * mm, "radius": 3.17 * mm});
            skCircle(sketch, "E4.0.15.16", {"center": v(393.7, 38.1) * mm, "radius": 3.17 * mm});
            skCircle(sketch, "E4.0.15.17", {"center": v(393.7, 12.7) * mm, "radius": 3.17 * mm});
            skCircle(sketch, "E4.0.16.8", {"center": v(419.1, 241.3) * mm, "radius": 3.17 * mm});
            skCircle(sketch, "E4.0.16.9", {"center": v(419.1, 215.9) * mm, "radius": 3.17 * mm});
            skCircle(sketch, "E4.0.16.10", {"center": v(419.1, 190.5) * mm, "radius": 3.17 * mm});
            skCircle(sketch, "E4.0.16.11", {"center": v(419.1, 165.1) * mm, "radius": 3.17 * mm});
            skCircle(sketch, "E4.0.16.12", {"center": v(419.1, 139.7) * mm, "radius": 3.17 * mm});
            skCircle(sketch, "E4.0.16.13", {"center": v(419.1, 114.3) * mm, "radius": 3.17 * mm});
            skCircle(sketch, "E4.0.16.14", {"center": v(419.1, 88.9) * mm, "radius": 3.17 * mm});
            skCircle(sketch, "E4.0.16.15", {"center": v(419.1, 63.5) * mm, "radius": 3.17 * mm});
            skCircle(sketch, "E4.0.16.16", {"center": v(419.1, 38.1) * mm, "radius": 3.17 * mm});
            skCircle(sketch, "E4.0.16.17", {"center": v(419.1, 12.7) * mm, "radius": 3.17 * mm});
            skCircle(sketch, "E4.0.17.8", {"center": v(444.5, 241.3) * mm, "radius": 3.17 * mm});
            skCircle(sketch, "E4.0.17.9", {"center": v(444.5, 215.9) * mm, "radius": 3.17 * mm});
            skCircle(sketch, "E4.0.17.10", {"center": v(444.5, 190.5) * mm, "radius": 3.17 * mm});
            skCircle(sketch, "E4.0.17.11", {"center": v(444.5, 165.1) * mm, "radius": 3.17 * mm});
            skCircle(sketch, "E4.0.17.12", {"center": v(444.5, 139.7) * mm, "radius": 3.17 * mm});
            skCircle(sketch, "E4.0.17.13", {"center": v(444.5, 114.3) * mm, "radius": 3.17 * mm});
            skCircle(sketch, "E4.0.17.14", {"center": v(444.5, 88.9) * mm, "radius": 3.17 * mm});
            skCircle(sketch, "E4.0.17.15", {"center": v(444.5, 63.5) * mm, "radius": 3.17 * mm});
            skCircle(sketch, "E4.0.17.16", {"center": v(444.5, 38.1) * mm, "radius": 3.17 * mm});
            skCircle(sketch, "E4.0.17.17", {"center": v(444.5, 12.7) * mm, "radius": 3.17 * mm});
            skCircle(sketch, "E4.0.18.8", {"center": v(469.9, 241.3) * mm, "radius": 3.17 * mm});
            skCircle(sketch, "E4.0.18.9", {"center": v(469.9, 215.9) * mm, "radius": 3.17 * mm});
            skCircle(sketch, "E4.0.18.10", {"center": v(469.9, 190.5) * mm, "radius": 3.17 * mm});
            skCircle(sketch, "E4.0.18.11", {"center": v(469.9, 165.1) * mm, "radius": 3.17 * mm});
            skCircle(sketch, "E4.0.18.12", {"center": v(469.9, 139.7) * mm, "radius": 3.17 * mm});
            skCircle(sketch, "E4.0.18.13", {"center": v(469.9, 114.3) * mm, "radius": 3.17 * mm});
            skCircle(sketch, "E4.0.18.14", {"center": v(469.9, 88.9) * mm, "radius": 3.17 * mm});
            skCircle(sketch, "E4.0.18.15", {"center": v(469.9, 63.5) * mm, "radius": 3.17 * mm});
            skCircle(sketch, "E4.0.18.16", {"center": v(469.9, 38.1) * mm, "radius": 3.17 * mm});
            skCircle(sketch, "E4.0.18.17", {"center": v(469.9, 12.7) * mm, "radius": 3.17 * mm});
            skCircle(sketch, "E4.0.19.8", {"center": v(495.3, 241.3) * mm, "radius": 3.17 * mm});
            skCircle(sketch, "E4.0.19.9", {"center": v(495.3, 215.9) * mm, "radius": 3.17 * mm});
            skCircle(sketch, "E4.0.19.10", {"center": v(495.3, 190.5) * mm, "radius": 3.17 * mm});
            skCircle(sketch, "E4.0.19.11", {"center": v(495.3, 165.1) * mm, "radius": 3.17 * mm});
            skCircle(sketch, "E4.0.19.12", {"center": v(495.3, 139.7) * mm, "radius": 3.17 * mm});
            skCircle(sketch, "E4.0.19.13", {"center": v(495.3, 114.3) * mm, "radius": 3.17 * mm});
            skCircle(sketch, "E4.0.19.14", {"center": v(495.3, 88.9) * mm, "radius": 3.17 * mm});
            skCircle(sketch, "E4.0.19.15", {"center": v(495.3, 63.5) * mm, "radius": 3.17 * mm});
            skCircle(sketch, "E4.0.19.16", {"center": v(495.3, 38.1) * mm, "radius": 3.17 * mm});
            skCircle(sketch, "E4.0.19.17", {"center": v(495.3, 12.7) * mm, "radius": 3.17 * mm});
            skCircle(sketch, "E4.0.20.8", {"center": v(520.7, 241.3) * mm, "radius": 3.17 * mm});
            skCircle(sketch, "E4.0.20.9", {"center": v(520.7, 215.9) * mm, "radius": 3.17 * mm});
            skCircle(sketch, "E4.0.20.10", {"center": v(520.7, 190.5) * mm, "radius": 3.17 * mm});
            skCircle(sketch, "E4.0.20.11", {"center": v(520.7, 165.1) * mm, "radius": 3.17 * mm});
            skCircle(sketch, "E4.0.20.12", {"center": v(520.7, 139.7) * mm, "radius": 3.17 * mm});
            skCircle(sketch, "E4.0.20.13", {"center": v(520.7, 114.3) * mm, "radius": 3.17 * mm});
            skCircle(sketch, "E4.0.20.14", {"center": v(520.7, 88.9) * mm, "radius": 3.17 * mm});
            skCircle(sketch, "E4.0.20.15", {"center": v(520.7, 63.5) * mm, "radius": 3.17 * mm});
            skCircle(sketch, "E4.0.20.16", {"center": v(520.7, 38.1) * mm, "radius": 3.17 * mm});
            skCircle(sketch, "E4.0.20.17", {"center": v(520.7, 12.7) * mm, "radius": 3.17 * mm});
            skCircle(sketch, "E4.0.21.8", {"center": v(546.1, 241.3) * mm, "radius": 3.17 * mm});
            skCircle(sketch, "E4.0.21.9", {"center": v(546.1, 215.9) * mm, "radius": 3.17 * mm});
            skCircle(sketch, "E4.0.21.10", {"center": v(546.1, 190.5) * mm, "radius": 3.17 * mm});
            skCircle(sketch, "E4.0.21.11", {"center": v(546.1, 165.1) * mm, "radius": 3.17 * mm});
            skCircle(sketch, "E4.0.21.12", {"center": v(546.1, 139.7) * mm, "radius": 3.17 * mm});
            skCircle(sketch, "E4.0.21.13", {"center": v(546.1, 114.3) * mm, "radius": 3.17 * mm});
            skCircle(sketch, "E4.0.21.14", {"center": v(546.1, 88.9) * mm, "radius": 3.17 * mm});
            skCircle(sketch, "E4.0.21.15", {"center": v(546.1, 63.5) * mm, "radius": 3.17 * mm});
            skCircle(sketch, "E4.0.21.16", {"center": v(546.1, 38.1) * mm, "radius": 3.17 * mm});
            skCircle(sketch, "E4.0.21.17", {"center": v(546.1, 12.7) * mm, "radius": 3.17 * mm});
            skCircle(sketch, "E4.0.22.8", {"center": v(571.5, 241.3) * mm, "radius": 3.17 * mm});
            skCircle(sketch, "E4.0.22.9", {"center": v(571.5, 215.9) * mm, "radius": 3.17 * mm});
            skCircle(sketch, "E4.0.22.10", {"center": v(571.5, 190.5) * mm, "radius": 3.17 * mm});
            skCircle(sketch, "E4.0.22.11", {"center": v(571.5, 165.1) * mm, "radius": 3.17 * mm});
            skCircle(sketch, "E4.0.22.12", {"center": v(571.5, 139.7) * mm, "radius": 3.17 * mm});
            skCircle(sketch, "E4.0.22.13", {"center": v(571.5, 114.3) * mm, "radius": 3.17 * mm});
            skCircle(sketch, "E4.0.22.14", {"center": v(571.5, 88.9) * mm, "radius": 3.17 * mm});
            skCircle(sketch, "E4.0.22.15", {"center": v(571.5, 63.5) * mm, "radius": 3.17 * mm});
            skCircle(sketch, "E4.0.22.16", {"center": v(571.5, 38.1) * mm, "radius": 3.17 * mm});
            skCircle(sketch, "E4.0.22.17", {"center": v(571.5, 12.7) * mm, "radius": 3.17 * mm});
            skCircle(sketch, "E4.0.23.8", {"center": v(596.9, 241.3) * mm, "radius": 3.17 * mm});
            skCircle(sketch, "E4.0.23.9", {"center": v(596.9, 215.9) * mm, "radius": 3.17 * mm});
            skCircle(sketch, "E4.0.23.10", {"center": v(596.9, 190.5) * mm, "radius": 3.17 * mm});
            skCircle(sketch, "E4.0.23.11", {"center": v(596.9, 165.1) * mm, "radius": 3.17 * mm});
            skCircle(sketch, "E4.0.23.12", {"center": v(596.9, 139.7) * mm, "radius": 3.17 * mm});
            skCircle(sketch, "E4.0.23.13", {"center": v(596.9, 114.3) * mm, "radius": 3.17 * mm});
            skCircle(sketch, "E4.0.23.14", {"center": v(596.9, 88.9) * mm, "radius": 3.17 * mm});
            skCircle(sketch, "E4.0.23.15", {"center": v(596.9, 63.5) * mm, "radius": 3.17 * mm});
            skCircle(sketch, "E4.0.23.16", {"center": v(596.9, 38.1) * mm, "radius": 3.17 * mm});
            skCircle(sketch, "E4.0.23.17", {"center": v(596.9, 12.7) * mm, "radius": 3.17 * mm});
            skCircle(sketch, "E5", {"center": v(25.4, 25.4) * mm, "radius": 3.18 * mm});
            skCircle(sketch, "E6", {"center": v(584.2, 25.4) * mm, "radius": 3.18 * mm});
            skCircle(sketch, "E7", {"center": v(584.2, 431.8) * mm, "radius": 3.18 * mm});
            skSolve(sketch);
        }
        {
            var Q0;
            Q0=makeQuery(id+"F0.imprint","IMPRINT",FACE,{"disambiguationData":[TD([[makeQuery(id+"F0.imprint","IMPRINT",EDGE,{"derivedFrom":sQuery(id+"F0.wireOp",EDGE,"E0.bottom")}),1.0]])]});
            extrude(context, id + "F1", {"entities" : qUnion([Q0]), "depth" : 12.7 * mm});
        }
        {
            var Q0;
            Q0=qCreatedBy(makeId("Front.planeOp"),FACE);
            var sketch = newSketch(context, id + "F2", { "sketchPlane" : qUnion([Q0])});
            skLineSegment(sketch, "E8", {"start": v(-422.09, 513.4) * mm, "end": v(-422.09, 223.4) * mm});
            skLineSegment(sketch, "E9", {"start": v(-422.09, 513.4) * mm, "end": v(-572.09, 513.4) * mm});
            skLineSegment(sketch, "E10", {"start": v(-572.09, 513.4) * mm, "end": v(-572.09, 300.79) * mm});
            skLineSegment(sketch, "E11", {"start": v(-572.09, 300.79) * mm, "end": v(-477.95, 300.79) * mm});
            skLineSegment(sketch, "E12", {"start": v(-477.95, 300.79) * mm, "end": v(-459.2, 223.4) * mm});
            skLineSegment(sketch, "E13", {"start": v(-459.2, 223.4) * mm, "end": v(-422.09, 223.4) * mm});
            skSolve(sketch);
        }
        {
            var Q0;
            Q0=makeQuery(id+"F2.imprint","IMPRINT",FACE,{"disambiguationData":[TD([[makeQuery(id+"F2.imprint","IMPRINT",EDGE,{"derivedFrom":sQuery(id+"F2.wireOp",EDGE,"E8")}),-1.0]])]});
            extrude(context, id + "F3", {"entities" : qUnion([Q0]), "depth" : 340 * mm});
        }
        {
            var Q0;
            Q0=qCreatedBy(makeId("Front.planeOp"),FACE);
            var sketch = newSketch(context, id + "F4", { "sketchPlane" : qUnion([Q0])});
            skLineSegment(sketch, "E14.bottom", {"start": v(-219.66, 255.79) * mm, "end": v(-149.66, 255.79) * mm});
            skLineSegment(sketch, "E14.top", {"start": v(-219.66, 130.79) * mm, "end": v(-149.66, 130.79) * mm});
            skLineSegment(sketch, "E14.left", {"start": v(-219.66, 255.79) * mm, "end": v(-219.66, 130.79) * mm});
            skLineSegment(sketch, "E14.right", {"start": v(-149.66, 255.79) * mm, "end": v(-149.66, 130.79) * mm});
            skSolve(sketch);
        }
        {
            var Q0;
            Q0 = qSketchRegion(id + "F4", true);
            extrude(context, id + "F5", {"entities" : qUnion([Q0]), "depth" : 350 * mm});
        }
        {
            var Q0;
            Q0=qCreatedBy(makeId("Top.planeOp"),FACE);
            var sketch = newSketch(context, id + "F6", { "sketchPlane" : qUnion([Q0])});
            skLineSegment(sketch, "E15.bottom", {"start": v(-437.41, 393.84) * mm, "end": v(-285.01, 393.84) * mm});
            skLineSegment(sketch, "E15.top", {"start": v(-437.41, 387.49) * mm, "end": v(-285.01, 387.49) * mm});
            skLineSegment(sketch, "E15.left", {"start": v(-437.41, 393.84) * mm, "end": v(-437.41, 387.49) * mm});
            skLineSegment(sketch, "E15.right", {"start": v(-285.01, 393.84) * mm, "end": v(-285.01, 387.49) * mm});
            skSolve(sketch);
        }
        {
            var Q0;
            Q0=makeQuery(id+"F6.imprint","IMPRINT",FACE,{"disambiguationData":[TD([[makeQuery(id+"F6.imprint","IMPRINT",EDGE,{"derivedFrom":sQuery(id+"F6.wireOp",EDGE,"E15.bottom")}),-1.0]])]});
            extrude(context, id + "F7", {"entities" : qUnion([Q0]), "depth" : 508 * mm, "offsetDistance" : 25.4 * mm});
        }
        {
            var Q0;
            Q0=qCreatedBy(makeId("Top.planeOp"),FACE);
            var sketch = newSketch(context, id + "F8", { "sketchPlane" : qUnion([Q0])});
            skLineSegment(sketch, "E16.bottom", {"start": v(750.73, -592.9) * mm, "end": v(141.13, -592.9) * mm});
            skLineSegment(sketch, "E16.top", {"start": v(750.73, -135.7) * mm, "end": v(141.13, -135.7) * mm});
            skLineSegment(sketch, "E16.left", {"start": v(750.73, -592.9) * mm, "end": v(750.73, -135.7) * mm});
            skLineSegment(sketch, "E16.right", {"start": v(141.13, -592.9) * mm, "end": v(141.13, -135.7) * mm});
            skCircle(sketch, "E17", {"center": v(166.53, -161.1) * mm, "radius": 3.18 * mm});
            skCircle(sketch, "E18", {"center": v(166.53, -567.5) * mm, "radius": 3.18 * mm});
            skCircle(sketch, "E19", {"center": v(725.33, -161.1) * mm, "radius": 3.18 * mm});
            skCircle(sketch, "E20", {"center": v(725.33, -567.5) * mm, "radius": 3.18 * mm});
            skSolve(sketch);
        }
        {
            var Q0;
            Q0=makeQuery(id+"F8.imprint","IMPRINT",FACE,{"disambiguationData":[TD([[makeQuery(id+"F8.imprint","IMPRINT",EDGE,{"derivedFrom":sQuery(id+"F8.wireOp",EDGE,"E16.bottom")}),-1.0]])]});
            extrude(context, id + "F9", {"entities" : qUnion([Q0]), "depth" : 6.35 * mm});
        }
        {
            var Q0;
            Q0=qCreatedBy(makeId("Front.planeOp"),FACE);
            var sketch = newSketch(context, id + "F10", { "sketchPlane" : qUnion([Q0])});
            skLineSegment(sketch, "E21.bottom", {"start": v(700.16, 488.95) * mm, "end": v(1119.26, 488.95) * mm});
            skLineSegment(sketch, "E21.top", {"start": v(700.16, 0) * mm, "end": v(1119.26, 0) * mm});
            skLineSegment(sketch, "E21.left", {"start": v(700.16, 488.95) * mm, "end": v(700.16, 0) * mm});
            skLineSegment(sketch, "E21.right", {"start": v(1119.26, 488.95) * mm, "end": v(1119.26, 0) * mm});
            skLineSegment(sketch, "E22.bottom", {"start": v(700.16, 488.95) * mm, "end": v(707.78, 488.95) * mm});
            skLineSegment(sketch, "E22.top", {"start": v(700.16, 481.33) * mm, "end": v(707.78, 481.33) * mm});
            skLineSegment(sketch, "E22.left", {"start": v(700.16, 488.95) * mm, "end": v(700.16, 481.33) * mm});
            skLineSegment(sketch, "E22.right", {"start": v(707.78, 488.95) * mm, "end": v(707.78, 481.33) * mm});
            skLineSegment(sketch, "E23.bottom", {"start": v(1119.26, 488.95) * mm, "end": v(1111.64, 488.95) * mm});
            skLineSegment(sketch, "E23.top", {"start": v(1119.26, 481.33) * mm, "end": v(1111.64, 481.33) * mm});
            skLineSegment(sketch, "E23.left", {"start": v(1119.26, 488.95) * mm, "end": v(1119.26, 481.33) * mm});
            skLineSegment(sketch, "E23.right", {"start": v(1111.64, 488.95) * mm, "end": v(1111.64, 481.33) * mm});
            skSolve(sketch);
        }
        {
            var Q0;
            {var subQ1=sQuery(id+"F10.wireOp",EDGE,"E21.top");Q0=makeQuery(id+"F10.imprint","IMPRINT",FACE,{"disambiguationData":[TD([[makeQuery(id+"F10.imprint","IMPRINT",EDGE,{"derivedFrom":subQ1}),1.0]])]});}
            extrude(context, id + "F11", {"entities" : qUnion([Q0]), "depth" : 6.35 * mm});
        }
        {
            var Q0;
            Q0=makeQuery(id+"F11.opExtrude","SWEPT_BODY",BODY,{"disambiguationData":[OSD([sQuery(id+"F10.wireOp",EDGE,"E21.bottom"),sQuery(id+"F10.wireOp",EDGE,"E21.top"),sQuery(id+"F10.wireOp",EDGE,"E21.left"),sQuery(id+"F10.wireOp",EDGE,"E21.right"),sQuery(id+"F10.wireOp",EDGE,"tZXS2C5H-MVHj-1kFy-8zpv-DSMq0DF46fty"),sQuery(id+"F10.wireOp",EDGE,"TfEHDnnW-syjM-KiiU-AfQn-d1ZEv0blvpZU"),sQuery(id+"F10.wireOp",EDGE,"nb2C3hCr-TuSM-aDbI-3AB1-IXlh67NKo5Lu"),sQuery(id+"F10.wireOp",EDGE,"3302ae05-356f-48ae-b5b1-42e5ac45e941.1.0.0"),sQuery(id+"F10.wireOp",EDGE,"3302ae05-356f-48ae-b5b1-42e5ac45e941.2.0.0"),sQuery(id+"F10.wireOp",EDGE,"3302ae05-356f-48ae-b5b1-42e5ac45e941.3.0.0"),sQuery(id+"F10.wireOp",EDGE,"3302ae05-356f-48ae-b5b1-42e5ac45e941.4.0.0"),sQuery(id+"F10.wireOp",EDGE,"3302ae05-356f-48ae-b5b1-42e5ac45e941.5.0.0"),sQuery(id+"F10.wireOp",EDGE,"3302ae05-356f-48ae-b5b1-42e5ac45e941.6.0.0"),sQuery(id+"F10.wireOp",EDGE,"3302ae05-356f-48ae-b5b1-42e5ac45e941.7.0.0"),sQuery(id+"F10.wireOp",EDGE,"3302ae05-356f-48ae-b5b1-42e5ac45e941.8.0.0")])]});
            transform(context, id + "F12", {"entities" : qUnion([Q0]), "transformType" : TransformType.TRANSLATION_3D, "dx" : 0 * mm, "dy" : 472.44 * mm, "dz" : 0 * mm, "makeCopy" : true});
        }
        {
            var Q0;
            Q0=makeQuery(id+"F11.opExtrude","CAP_FACE",FACE,{"disambiguationData":[OSD([sQuery(id+"F10.wireOp",EDGE,"E21.bottom"),sQuery(id+"F10.wireOp",EDGE,"E21.top"),sQuery(id+"F10.wireOp",EDGE,"E21.left"),sQuery(id+"F10.wireOp",EDGE,"E21.right"),sQuery(id+"F10.wireOp",EDGE,"tZXS2C5H-MVHj-1kFy-8zpv-DSMq0DF46fty"),sQuery(id+"F10.wireOp",EDGE,"TfEHDnnW-syjM-KiiU-AfQn-d1ZEv0blvpZU")])],"isStart":false});
            var sketch = newSketch(context, id + "F13", { "sketchPlane" : qUnion([Q0])});
            skCircle(sketch, "E24", {"center": v(808.1, 450.85) * mm, "radius": 4.76 * mm});
            skCircle(sketch, "E25.1.0.0", {"center": v(833.5, 450.85) * mm, "radius": 4.76 * mm});
            skCircle(sketch, "E25.2.0.0", {"center": v(858.9, 450.85) * mm, "radius": 4.76 * mm});
            skCircle(sketch, "E25.3.0.0", {"center": v(884.3, 450.85) * mm, "radius": 4.76 * mm});
            skCircle(sketch, "E25.4.0.0", {"center": v(909.7, 450.85) * mm, "radius": 4.76 * mm});
            skCircle(sketch, "E25.5.0.0", {"center": v(935.1, 450.85) * mm, "radius": 4.76 * mm});
            skCircle(sketch, "E25.6.0.0", {"center": v(960.5, 450.85) * mm, "radius": 4.76 * mm});
            skCircle(sketch, "E25.7.0.0", {"center": v(985.9, 450.85) * mm, "radius": 4.76 * mm});
            skCircle(sketch, "E25.8.0.0", {"center": v(1011.3, 450.85) * mm, "radius": 4.76 * mm});
            skLineSegment(sketch, "E25.direction1", {"start": v(808.1, 450.85) * mm, "end": v(833.5, 450.85) * mm, "construction": true});
            skLineSegment(sketch, "E26", {"start": v(909.7, 450.85) * mm, "end": v(909.7, 488.95) * mm, "construction": true});
            skLineSegment(sketch, "E27.bottom", {"start": v(782.7, 468.25) * mm, "end": v(1036.7, 468.25) * mm, "construction": true});
            skLineSegment(sketch, "E27.top", {"start": v(782.7, 433.45) * mm, "end": v(1036.7, 433.45) * mm, "construction": true});
            skLineSegment(sketch, "E27.left", {"start": v(782.7, 468.25) * mm, "end": v(782.7, 433.45) * mm, "construction": true});
            skLineSegment(sketch, "E27.right", {"start": v(1036.7, 468.25) * mm, "end": v(1036.7, 433.45) * mm, "construction": true});
            skLineSegment(sketch, "E28", {"start": v(909.7, 450.85) * mm, "end": v(909.7, 433.45) * mm, "construction": true});
            skLineSegment(sketch, "E29", {"start": v(1011.3, 450.85) * mm, "end": v(1036.7, 450.85) * mm, "construction": true});
            skCircle(sketch, "E30", {"center": v(782.7, 468.25) * mm, "radius": 9.23 * mm});
            skCircle(sketch, "E31", {"center": v(782.7, 433.45) * mm, "radius": 9.23 * mm});
            skCircle(sketch, "E32", {"center": v(1036.7, 468.25) * mm, "radius": 9.23 * mm});
            skCircle(sketch, "E33", {"center": v(1036.7, 433.45) * mm, "radius": 9.23 * mm});
            skSolve(sketch);
        }
        {
            var Q0;
            Q0 = qSketchRegion(id + "F13", true);
            extrude(context, id + "F14", {"entities" : qUnion([Q0]), "operationType" : NewBodyOperationType.REMOVE, "oppositeDirection" : true, "depth" : 25.4 * mm});
        }
        {
            var Q0;
            Q0=makeQuery(id+"F12.opPattern","COPY",BODY,{"derivedFrom":makeQuery(id+"F11.opExtrude","SWEPT_BODY",BODY,{"disambiguationData":[OSD([sQuery(id+"F10.wireOp",EDGE,"E21.bottom"),sQuery(id+"F10.wireOp",EDGE,"E21.top"),sQuery(id+"F10.wireOp",EDGE,"E21.left"),sQuery(id+"F10.wireOp",EDGE,"E21.right"),sQuery(id+"F10.wireOp",EDGE,"tZXS2C5H-MVHj-1kFy-8zpv-DSMq0DF46fty"),sQuery(id+"F10.wireOp",EDGE,"TfEHDnnW-syjM-KiiU-AfQn-d1ZEv0blvpZU")])]}),"instanceName":"1"});
            transform(context, id + "F15", {"entities" : qUnion([Q0]), "transformType" : TransformType.TRANSLATION_3D, "dx" : 579.12 * mm, "dy" : 0 * mm, "dz" : 0 * mm, "makeCopy" : true});
        }
        {
            var Q0;
            Q0=makeQuery(id+"F15.opPattern","COPY",FACE,{"derivedFrom":makeQuery(id+"F12.opPattern","COPY",FACE,{"derivedFrom":makeQuery(id+"F11.opExtrude","CAP_FACE",FACE,{"disambiguationData":[OSD([sQuery(id+"F10.wireOp",EDGE,"E21.bottom"),sQuery(id+"F10.wireOp",EDGE,"E21.top"),sQuery(id+"F10.wireOp",EDGE,"E21.left"),sQuery(id+"F10.wireOp",EDGE,"E21.right"),sQuery(id+"F10.wireOp",EDGE,"tZXS2C5H-MVHj-1kFy-8zpv-DSMq0DF46fty"),sQuery(id+"F10.wireOp",EDGE,"TfEHDnnW-syjM-KiiU-AfQn-d1ZEv0blvpZU")])],"isStart":false}),"instanceName":"1"}),"instanceName":"1"});
            var sketch = newSketch(context, id + "F16", { "sketchPlane" : qUnion([Q0])});
            skLineSegment(sketch, "E34.bottom", {"start": v(1412.63, 152.4) * mm, "end": v(1565.03, 152.4) * mm});
            skLineSegment(sketch, "E34.top", {"start": v(1412.63, 50.8) * mm, "end": v(1565.03, 50.8) * mm});
            skLineSegment(sketch, "E34.left", {"start": v(1387.23, 127) * mm, "end": v(1387.23, 76.2) * mm});
            skLineSegment(sketch, "E34.right", {"start": v(1590.43, 127) * mm, "end": v(1590.43, 76.2) * mm});
            skPoint(sketch, "E34.middle", {"position": v(1488.83, 101.6) * mm});
            skPoint(sketch, "E35.visualSharp", {"position": v(1387.23, 152.4) * mm});
            skArc(sketch, "E35.filletArc", {"start": v(1412.63, 152.4) * mm, "mid": v(1394.67, 144.96) * mm, "end": v(1387.23, 127) * mm});
            skPoint(sketch, "E36.visualSharp", {"position": v(1590.43, 152.4) * mm});
            skArc(sketch, "E36.filletArc", {"start": v(1590.43, 127) * mm, "mid": v(1582.99, 144.96) * mm, "end": v(1565.03, 152.4) * mm});
            skPoint(sketch, "E37.visualSharp", {"position": v(1387.23, 50.8) * mm});
            skArc(sketch, "E37.filletArc", {"start": v(1387.23, 76.2) * mm, "mid": v(1394.67, 58.24) * mm, "end": v(1412.63, 50.8) * mm});
            skPoint(sketch, "E38.visualSharp", {"position": v(1590.43, 50.8) * mm});
            skArc(sketch, "E38.filletArc", {"start": v(1565.03, 50.8) * mm, "mid": v(1582.99, 58.24) * mm, "end": v(1590.43, 76.2) * mm});
            skLineSegment(sketch, "E39", {"start": v(1488.83, 101.6) * mm, "end": v(1488.83, 0) * mm, "construction": true});
            skSolve(sketch);
        }
        {
            var Q0;
            Q0=makeQuery(id+"F16.imprint","IMPRINT",FACE,{"disambiguationData":[TD([[makeQuery(id+"F16.imprint","IMPRINT",EDGE,{"derivedFrom":sQuery(id+"F16.wireOp",EDGE,"E34.bottom")}),-1.0]])]});
            extrude(context, id + "F17", {"entities" : qUnion([Q0]), "operationType" : NewBodyOperationType.REMOVE, "oppositeDirection" : true, "depth" : 25.4 * mm});
        }
        {
            var Q0;
            Q0=qCreatedBy(makeId("Top.planeOp"),FACE);
            var sketch = newSketch(context, id + "F18", { "sketchPlane" : qUnion([Q0])});
            skLineSegment(sketch, "E40.bottom", {"start": v(-620.92, -317.1) * mm, "end": v(-189.12, -317.1) * mm});
            skLineSegment(sketch, "E40.top", {"start": v(-620.92, -748.9) * mm, "end": v(-189.12, -748.9) * mm});
            skLineSegment(sketch, "E40.left", {"start": v(-620.92, -317.1) * mm, "end": v(-620.92, -748.9) * mm});
            skLineSegment(sketch, "E40.right", {"start": v(-189.12, -317.1) * mm, "end": v(-189.12, -748.9) * mm});
            skArc(sketch, "E41", {"start": v(-214.52, -317.1) * mm, "mid": v(-207.08, -335.06) * mm, "end": v(-189.12, -342.5) * mm});
            skArc(sketch, "E42", {"start": v(-595.52, -317.1) * mm, "mid": v(-602.96, -335.06) * mm, "end": v(-620.92, -342.5) * mm});
            skArc(sketch, "E43", {"start": v(-189.12, -723.5) * mm, "mid": v(-207.08, -730.94) * mm, "end": v(-214.52, -748.9) * mm});
            skArc(sketch, "E44", {"start": v(-620.92, -723.5) * mm, "mid": v(-602.96, -730.94) * mm, "end": v(-595.52, -748.9) * mm});
            skSolve(sketch);
        }
        {
            var Q0;
            {var subQ0=sQuery(id+"F18.wireOp",EDGE,"E41");Q0=makeQuery(id+"F18.imprint","IMPRINT",FACE,{"disambiguationData":[TD([[makeQuery(id+"F18.imprint","IMPRINT",EDGE,{"derivedFrom":subQ0}),-1.0]])]});}
            extrude(context, id + "F19", {"entities" : qUnion([Q0]), "depth" : 6.35 * mm});
        }
        {
            var Q0;
            Q0=qCreatedBy(makeId("Front.planeOp"),FACE);
            var sketch = newSketch(context, id + "F20", { "sketchPlane" : qUnion([Q0])});
            skLineSegment(sketch, "E45.bottom", {"start": v(1752.13, 152.4) * mm, "end": v(1955.33, 152.4) * mm});
            skLineSegment(sketch, "E45.top", {"start": v(1752.13, 0) * mm, "end": v(1955.33, 0) * mm});
            skLineSegment(sketch, "E45.left", {"start": v(1726.73, 127) * mm, "end": v(1726.73, 25.4) * mm});
            skLineSegment(sketch, "E45.right", {"start": v(1980.73, 127) * mm, "end": v(1980.73, 25.4) * mm});
            skPoint(sketch, "E46.visualSharp", {"position": v(1726.73, 152.4) * mm});
            skArc(sketch, "E46.filletArc", {"start": v(1752.13, 152.4) * mm, "mid": v(1734.17, 144.96) * mm, "end": v(1726.73, 127) * mm});
            skPoint(sketch, "E47.visualSharp", {"position": v(1726.73, 0) * mm});
            skArc(sketch, "E47.filletArc", {"start": v(1726.73, 25.4) * mm, "mid": v(1734.17, 7.44) * mm, "end": v(1752.13, 0) * mm});
            skPoint(sketch, "E48.visualSharp", {"position": v(1980.73, 152.4) * mm});
            skArc(sketch, "E48.filletArc", {"start": v(1980.73, 127) * mm, "mid": v(1973.3, 144.96) * mm, "end": v(1955.33, 152.4) * mm});
            skPoint(sketch, "E49.visualSharp", {"position": v(1980.73, 0) * mm});
            skArc(sketch, "E49.filletArc", {"start": v(1955.33, 0) * mm, "mid": v(1973.3, 7.44) * mm, "end": v(1980.73, 25.4) * mm});
            skSolve(sketch);
        }
        {
            var Q0;
            Q0=makeQuery(id+"F20.imprint","IMPRINT",FACE,{"disambiguationData":[TD([[makeQuery(id+"F20.imprint","IMPRINT",EDGE,{"derivedFrom":sQuery(id+"F20.wireOp",EDGE,"E45.bottom")}),-1.0]])]});
            extrude(context, id + "F21", {"entities" : qUnion([Q0]), "depth" : 6.35 * mm});
        }
        {
            var Q0;
            Q0=makeQuery(id+"F15.opPattern","COPY",FACE,{"derivedFrom":makeQuery(id+"F12.opPattern","COPY",FACE,{"derivedFrom":makeQuery(id+"F11.opExtrude","CAP_FACE",FACE,{"disambiguationData":[OSD([sQuery(id+"F10.wireOp",EDGE,"E21.bottom"),sQuery(id+"F10.wireOp",EDGE,"E21.top"),sQuery(id+"F10.wireOp",EDGE,"E21.left"),sQuery(id+"F10.wireOp",EDGE,"E21.right"),sQuery(id+"F10.wireOp",EDGE,"E22.top"),sQuery(id+"F10.wireOp",EDGE,"E22.right"),sQuery(id+"F10.wireOp",EDGE,"E23.top"),sQuery(id+"F10.wireOp",EDGE,"E23.right")])],"isStart":false}),"instanceName":"1"}),"instanceName":"1"});
            var sketch = newSketch(context, id + "F22", { "sketchPlane" : qUnion([Q0])});
            skLineSegment(sketch, "E50.bottom", {"start": v(1698.38, 0) * mm, "end": v(1717.43, 0) * mm});
            skLineSegment(sketch, "E50.top", {"start": v(1698.38, 488.95) * mm, "end": v(1717.43, 488.95) * mm});
            skLineSegment(sketch, "E50.left", {"start": v(1698.38, 0) * mm, "end": v(1698.38, 488.95) * mm});
            skLineSegment(sketch, "E50.right", {"start": v(1717.43, 0) * mm, "end": v(1717.43, 488.95) * mm});
            skLineSegment(sketch, "E51.bottom", {"start": v(1279.28, 0) * mm, "end": v(1260.23, 0) * mm});
            skLineSegment(sketch, "E51.top", {"start": v(1279.28, 488.95) * mm, "end": v(1260.23, 488.95) * mm});
            skLineSegment(sketch, "E51.left", {"start": v(1279.28, 0) * mm, "end": v(1279.28, 488.95) * mm});
            skLineSegment(sketch, "E51.right", {"start": v(1260.23, 0) * mm, "end": v(1260.23, 488.95) * mm});
            skLineSegment(sketch, "E52.bottom", {"start": v(1279.28, 488.95) * mm, "end": v(1286.9, 488.95) * mm});
            skLineSegment(sketch, "E52.top", {"start": v(1279.28, 481.33) * mm, "end": v(1286.9, 481.33) * mm});
            skLineSegment(sketch, "E52.left", {"start": v(1279.28, 488.95) * mm, "end": v(1279.28, 481.33) * mm});
            skLineSegment(sketch, "E52.right", {"start": v(1286.9, 488.95) * mm, "end": v(1286.9, 481.33) * mm});
            skLineSegment(sketch, "E53.bottom", {"start": v(1690.76, 481.33) * mm, "end": v(1698.38, 481.33) * mm});
            skLineSegment(sketch, "E53.top", {"start": v(1690.76, 488.95) * mm, "end": v(1698.38, 488.95) * mm});
            skLineSegment(sketch, "E53.left", {"start": v(1690.76, 481.33) * mm, "end": v(1690.76, 488.95) * mm});
            skLineSegment(sketch, "E53.right", {"start": v(1698.38, 481.33) * mm, "end": v(1698.38, 488.95) * mm});
            skLineSegment(sketch, "E54.bottom", {"start": v(1717.43, 488.95) * mm, "end": v(1260.23, 488.95) * mm});
            skLineSegment(sketch, "E54.top", {"start": v(1717.43, 508) * mm, "end": v(1260.23, 508) * mm});
            skLineSegment(sketch, "E54.left", {"start": v(1717.43, 488.95) * mm, "end": v(1717.43, 508) * mm});
            skLineSegment(sketch, "E54.right", {"start": v(1260.23, 488.95) * mm, "end": v(1260.23, 508) * mm});
            skSolve(sketch);
        }
        {
            var Q0;
            Q0 = qSketchRegion(id + "F22", true);
            var Q1;
            Q1=makeQuery(id+"F15.opPattern","COPY",FACE,{"derivedFrom":makeQuery(id+"F12.opPattern","COPY",FACE,{"derivedFrom":makeQuery(id+"F11.opExtrude","CAP_FACE",FACE,{"disambiguationData":[OSD([sQuery(id+"F10.wireOp",EDGE,"E21.bottom"),sQuery(id+"F10.wireOp",EDGE,"E21.top"),sQuery(id+"F10.wireOp",EDGE,"E21.left"),sQuery(id+"F10.wireOp",EDGE,"E21.right"),sQuery(id+"F10.wireOp",EDGE,"E22.top"),sQuery(id+"F10.wireOp",EDGE,"E22.right"),sQuery(id+"F10.wireOp",EDGE,"E23.top"),sQuery(id+"F10.wireOp",EDGE,"E23.right")])],"isStart":true}),"instanceName":"1"}),"instanceName":"1"});
            extrude(context, id + "F23", {"entities" : qUnion([Q0]), "operationType" : NewBodyOperationType.ADD, "endBound" : BoundingType.UP_TO_SURFACE, "oppositeDirection" : true, "endBoundEntityFace" : qUnion([Q1]), "depth" : 25.4 * mm});
        }
        {
            var Q0;
            Q0=makeQuery(id+"F23.boolean.opBoolean","MERGE",FACE,{"derivedFrom":[makeQuery(id+"F15.opPattern","COPY",FACE,{"derivedFrom":makeQuery(id+"F12.opPattern","COPY",FACE,{"derivedFrom":makeQuery(id+"F11.opExtrude","CAP_FACE",FACE,{"disambiguationData":[OSD([sQuery(id+"F10.wireOp",EDGE,"E21.bottom"),sQuery(id+"F10.wireOp",EDGE,"E21.top"),sQuery(id+"F10.wireOp",EDGE,"E21.left"),sQuery(id+"F10.wireOp",EDGE,"E21.right"),sQuery(id+"F10.wireOp",EDGE,"E22.top"),sQuery(id+"F10.wireOp",EDGE,"E22.right"),sQuery(id+"F10.wireOp",EDGE,"E23.top"),sQuery(id+"F10.wireOp",EDGE,"E23.right")])],"isStart":false}),"instanceName":"1"}),"instanceName":"1"}),makeQuery(id+"F23.opExtrude","CAP_FACE",FACE,{"disambiguationData":[OSD([sQuery(id+"F22.wireOp",EDGE,"E50.bottom"),sQuery(id+"F22.wireOp",EDGE,"E50.left"),sQuery(id+"F22.wireOp",EDGE,"E50.right"),sQuery(id+"F22.wireOp",EDGE,"E51.bottom"),sQuery(id+"F22.wireOp",EDGE,"E51.left"),sQuery(id+"F22.wireOp",EDGE,"E51.right"),sQuery(id+"F22.wireOp",EDGE,"E52.top"),sQuery(id+"F22.wireOp",EDGE,"E52.right"),sQuery(id+"F22.wireOp",EDGE,"E53.bottom"),sQuery(id+"F22.wireOp",EDGE,"E53.left"),sQuery(id+"F22.wireOp",EDGE,"E54.bottom"),sQuery(id+"F22.wireOp",EDGE,"E54.top"),sQuery(id+"F22.wireOp",EDGE,"E54.left"),sQuery(id+"F22.wireOp",EDGE,"E54.right")])],"isStart":true})]});
            var sketch = newSketch(context, id + "F24", { "sketchPlane" : qUnion([Q0])});
            skCircle(sketch, "E55", {"center": v(1294.52, 457.2) * mm, "radius": 3.18 * mm});
            skCircle(sketch, "E56", {"center": v(1294.52, 12.7) * mm, "radius": 3.18 * mm});
            skCircle(sketch, "E57", {"center": v(1683.14, 457.2) * mm, "radius": 3.18 * mm});
            skCircle(sketch, "E58", {"center": v(1683.14, 12.7) * mm, "radius": 3.18 * mm});
            skCircle(sketch, "E59", {"center": v(1412.63, 473.71) * mm, "radius": 3.18 * mm});
            skCircle(sketch, "E60", {"center": v(1565.03, 473.71) * mm, "radius": 3.18 * mm});
            skCircle(sketch, "E61", {"center": v(1294.52, 234.95) * mm, "radius": 3.18 * mm});
            skCircle(sketch, "E62", {"center": v(1683.14, 234.95) * mm, "radius": 3.18 * mm});
            skLineSegment(sketch, "E63", {"start": v(1683.14, 12.7) * mm, "end": v(1683.14, 457.2) * mm, "construction": true});
            skLineSegment(sketch, "E64", {"start": v(1294.52, 457.2) * mm, "end": v(1294.52, 12.7) * mm, "construction": true});
            skLineSegment(sketch, "E65", {"start": v(1683.14, 12.7) * mm, "end": v(1294.52, 12.7) * mm, "construction": true});
            skLineSegment(sketch, "E66", {"start": v(1683.14, 457.2) * mm, "end": v(1294.52, 457.2) * mm, "construction": true});
            skLineSegment(sketch, "E67", {"start": v(1412.63, 473.71) * mm, "end": v(1565.03, 473.71) * mm, "construction": true});
            skLineSegment(sketch, "E68", {"start": v(1488.83, 473.71) * mm, "end": v(1488.83, 508) * mm, "construction": true});
            skSolve(sketch);
        }
        {
            var Q0;
            Q0 = qSketchRegion(id + "F24", true);
            extrude(context, id + "F25", {"entities" : qUnion([Q0]), "operationType" : NewBodyOperationType.REMOVE, "oppositeDirection" : true, "depth" : 25.4 * mm, "offsetDistance" : 25.4 * mm});
        }
    });
